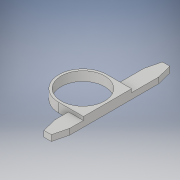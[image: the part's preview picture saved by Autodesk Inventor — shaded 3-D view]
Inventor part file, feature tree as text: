
AUTODESK INVENTOR PART (.ipt)
format: ipt  version: 2019 (Build 230136000, 136)  size: 135,680 bytes
history: native  units: mm
features: extrude x3, sketch x3
ambient origin geometry x8: Origin, YZ Plane, XZ Plane, XY Plane, X Axis, Y Axis, Z Axis, Center Point
bodies: Solid1 (feature_tree)
feature tree (6):
  extrude  "Extrusion1"  Depth=3.2mm
  extrude  "Extrusion2"  Depth=12.8mm
  extrude  "Extrusion3"  Depth=1.27mm TaperAngle=0.0deg
  sketch  "Sketch1"  dims[d0=25.6mm d1=3.2mm]
  sketch  "Sketch4"  dims[d2=1.6mm d3=12.8mm]
  sketch  "Sketch5"  dims[d4=3.2mm d5=1.27mm d6=0.0mm d12=0.0mm d23=10.4mm d24=0.0mm d27=5.3mm d28=2.0mm d29=0.0mm d30=9.4mm d31=5.3mm d32=5.2mm d33=2.0mm d34=0.0mm]
